# Revit family: Paper Dispenser and Waste_Metlam_Recessed_6.5L Waste
name_source: partatom
category: Specialty Equipment
revit_build: Autodesk Revit 2016 (Build: 20170117_1200(x64)
units: mm (PartAtom-declared; Revit-internal decimal feet)

## family parameters
Always vertical = Yes
Cut with Voids When Loaded = Yes
OmniClass Number = 23.40.20.21.17
OmniClass Title = Paper Towel Dispensers, Disposal Units
Part Type = Normal
Room Calculation Point = Yes
Round Connector Dimension = Use Diameter
Shared = No
Work Plane-Based = No

## types (1)
- 365w x 112d x 720h (ML710_RECMK2)
    Description = Paper Towel Dispenser & Waste Receptacle
Paper Towel Dispenser & Waste Receptacle
Paper Towel Dispenser & Waste Receptacle
Paper Towel Dispenser & Waste Receptacle - Recessed
    Manufacturer = Metlam
    Manufacturer_Overall Depth = 112 mm  [stored 0.367454 ft]
    Manufacturer_Overall Height = 720 mm  [stored 2.3622 ft]
    Manufacturer_Overall Width = 365 mm  [stored 1.19751 ft]
    Manufacturer_Spec Code = ML710_RECMK2
    Manufacturer_URL__Product Specific = https://metlam.com.au
    Material_ANZRS = z_Metlam_Metal_Stainless Steel_Satin
    Model = ML710_RECMK2
    Type Comments = 2 in 1 Combo Units
    URL = http://www.metlam.com.au

note: [stored X ft] marks values corroborated as IEEE doubles in the binary element streams (Revit-internal decimal feet)

## geometry (parser evidence)
native form markers: Sweep x3
no freeform markers — native parametric forms only
